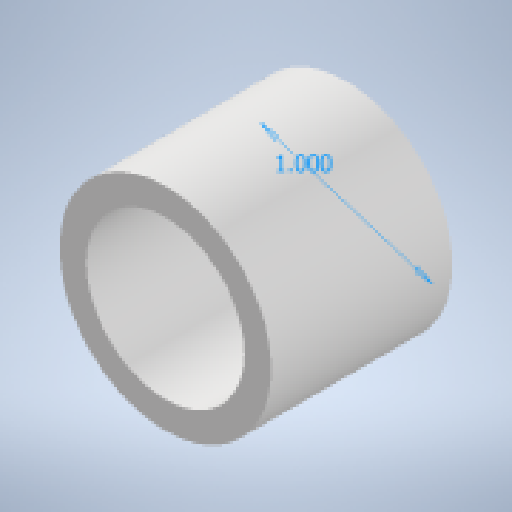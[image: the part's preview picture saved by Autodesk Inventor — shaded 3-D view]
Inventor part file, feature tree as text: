
AUTODESK INVENTOR PART (.ipt)
format: ipt  version: 2024 (Build 280153000, 153)  size: 145,920 bytes
history: native  units: in
note: dims shown in document units (in); Inventor stores cm internally (conversion verified against a paired STEP export)
features: extrude x1, sketch x1
ambient origin geometry x8: Origin, YZ Plane, XZ Plane, XY Plane, X Axis, Y Axis, Z Axis, Center Point
bodies: Solid1 (feature_tree)
feature tree (2):
  extrude  "Extrusion1"  [1 undecoded]
  sketch  "Sketch1"  dims[d0=1.0in d1=0.0in]
note: 1 required parameter value undecoded (feature->parameter linkage not recoverable at this tier; creation-order binding heuristic only, values carry confidence <= 0.55)
